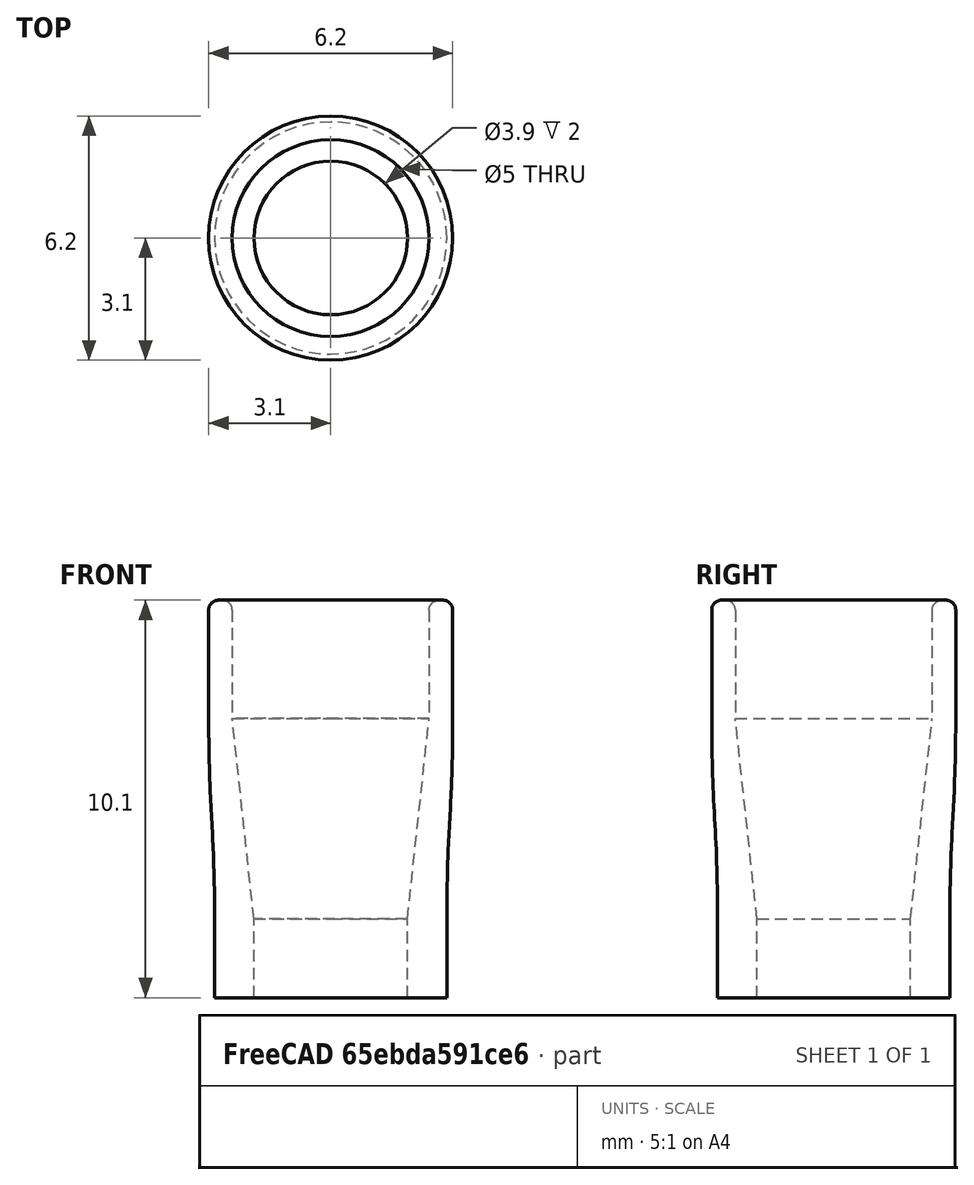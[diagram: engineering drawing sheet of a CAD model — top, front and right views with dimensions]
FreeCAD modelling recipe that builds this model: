
FCSTD DOCUMENT  (FreeCAD 0.18R16093 (Git))
Label: MagnetHolderOld
License: All rights reserved
LicenseURL: http://en.wikipedia.org/wiki/All_rights_reserved
objects: Sketcher::SketchObject×1, PartDesign::Revolution×1, PartDesign::Body×1
note: 4 computed .brp shape members not serialized (recipe doc carries the construction recipe); baked Part::Feature solids carry a one-line shape summary decoded from their .brp

FEATURE [Sketcher::SketchObject] Sketch
  MapMode = 5
  Placement = pos=(0,0,0) rot=(0.57735,0.57735,0.57735;2.0944rad)
  Support = -> [YZ_Plane]
  sketch-geometry (13):
    g0: LineSegment [constr] StartX=-1.95 StartY=-2 StartZ=0 EndX=0 EndY=-2 EndZ=0
    g1: LineSegment StartX=-1.95 StartY=-2 StartZ=0 EndX=-1.95 EndY=0 EndZ=0
    g2: LineSegment StartX=-2.5 StartY=7.85 StartZ=0 EndX=-2.5 EndY=5.1 EndZ=0
    g3: LineSegment StartX=-1.95 StartY=0 StartZ=0 EndX=-2.5 EndY=5.1 EndZ=0
    g4: LineSegment StartX=-2.75 StartY=8.1 StartZ=0 EndX=-2.85 EndY=8.1 EndZ=0
    g5: LineSegment StartX=-1.95 StartY=-2 StartZ=0 EndX=-2.95 EndY=-2 EndZ=0
    g6: LineSegment StartX=-2.95 StartY=-2 StartZ=0 EndX=-2.95 EndY=0 EndZ=0
    g7: LineSegment StartX=-3.1 StartY=7.85 StartZ=0 EndX=-3.1 EndY=5.1 EndZ=0
    g8: LineSegment [constr] StartX=-3.1 StartY=5.1 StartZ=0 EndX=-2.5 EndY=5.1 EndZ=0
    g9: ArcOfCircle CenterX=-2.85 CenterY=7.85 CenterZ=0 NormalX=0 NormalY=0 NormalZ=1 AngleXU=0 Radius=0.25 StartAngle=1.5708 EndAngle=3.14159
    g10: ArcOfCircle CenterX=40.2875 CenterY=5.1 CenterZ=0 NormalX=0 NormalY=0 NormalZ=1 AngleXU=0 Radius=43.3875 StartAngle=3.14159 EndAngle=3.2004
    g11: ArcOfCircle CenterX=-46.3375 CenterY=0 CenterZ=0 NormalX=0 NormalY=0 NormalZ=1 AngleXU=0 Radius=43.3875 StartAngle=0 EndAngle=0.0588066
    g12: ArcOfCircle CenterX=-2.75 CenterY=7.85 CenterZ=0 NormalX=0 NormalY=0 NormalZ=1 AngleXU=0 Radius=0.25 StartAngle=7e-16 EndAngle=1.5708
  constraints (35):
    c: Horizontal(g0)
    c: Coincident(g1,g0)
    c: PointOnObject(g1,g-1)
    c: Vertical(g1)
    c: PointOnObject(g0,g-2)
    c: Vertical(g2)
    c: Coincident(g3,g1)
    c: Coincident(g3,g2)
    c: DistanceX(g0,g0) = 1.95
    c: DistanceY(g0,g1) = 2
    c: Horizontal(g4)
    c: Coincident(g5,g1)
    c: Horizontal(g5)
    c: Vertical(g6)
    c: Vertical(g7)
    c: PointOnObject(g6,g-1)
    c: Coincident(g8,g7)
    c: Coincident(g8,g2)
    c: Horizontal(g8)
    c: Tangent(g7,g9) = -1.5708
    c: Tangent(g4,g9) = -1.5708
    c: Radius(g9) = 0.25
    c: DistanceX(g6,g1) = 1
    c: Coincident(g6,g5)
    c: Tangent(g11,g6) = -1.5708
    c: Tangent(g11,g10) = 1.5708
    c: Tangent(g10,g7) = -1.5708
    c: Equal(g11,g10)
    c: Tangent(g4,g12) = -1.5708
    c: Tangent(g2,g12) = 1.5708
    c: Radius(g12) = 0.25
    c: DistanceY(g1,g4) = 8.1
    c: DistanceX(g2,g-1) = 2.5
    c: DistanceY(g2,g4) = 3
    c: DistanceX(g7,g2) = 0.6
FEATURE [PartDesign::Revolution] Revolution
  Angle = 360
  Axis = (-2e-16,3e-16,1)
  Base = (0,0,0)
  Placement = pos=(0,0,0) rot=(0.57735,0.57735,0.57735;2.0944rad)
  Profile = -> Sketch
  ReferenceAxis = -> Sketch [V_Axis]
FEATURE [PartDesign::Body] Body
  Group = -> [Sketch,Revolution]
  Origin = -> Origin
  Tip = -> Revolution
